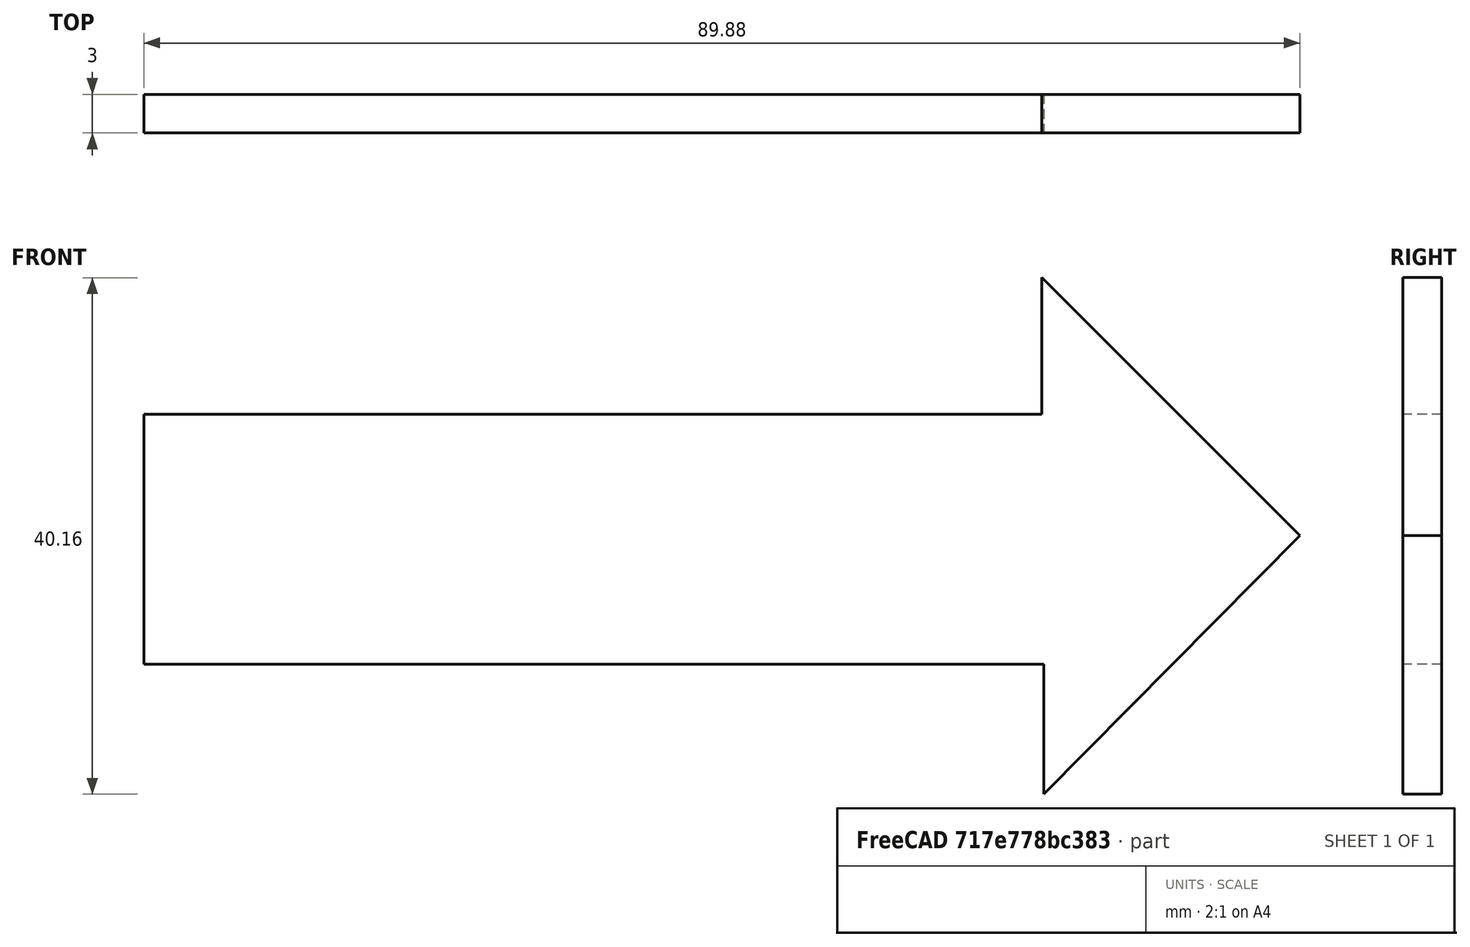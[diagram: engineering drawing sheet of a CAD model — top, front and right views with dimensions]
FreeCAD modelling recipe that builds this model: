
FCSTD DOCUMENT  (FreeCAD 0.21R33694 (Git))
Label: OJT1_T16R02.fletxa
License: All rights reserved
LicenseURL: http://en.wikipedia.org/wiki/All_rights_reserved
objects: Sketcher::SketchObject×1, PartDesign::Pad×1, PartDesign::Body×1
note: 4 computed .brp shape members not serialized (recipe doc carries the construction recipe); baked Part::Feature solids carry a one-line shape summary decoded from their .brp

FEATURE [Sketcher::SketchObject] Sketch
  FullyConstrained = false
  MapMode = 5
  Placement = pos=(0,0,0) rot=(1,0,0;1.5708rad)
  Support = -> [XZ_Plane]
  sketch-geometry (7):
    g0: LineSegment StartX=-29.9479 StartY=9.40476 StartZ=0 EndX=39.8524 EndY=9.40476 EndZ=0
    g1: LineSegment StartX=39.8524 StartY=9.40476 StartZ=0 EndX=39.8524 EndY=20.0415 EndZ=0
    g2: LineSegment StartX=39.8524 StartY=20.0415 StartZ=0 EndX=59.9287 EndY=0 EndZ=0
    g3: LineSegment StartX=59.9287 StartY=0 StartZ=0 EndX=40.0154 EndY=-20.1171 EndZ=0
    g4: LineSegment StartX=40.0154 StartY=-20.1171 StartZ=0 EndX=40.0154 EndY=-10.0238 EndZ=0
    g5: LineSegment StartX=40.0154 StartY=-10.0238 StartZ=0 EndX=-29.9479 EndY=-10.0238 EndZ=0
    g6: LineSegment StartX=-29.9479 StartY=-10.0238 StartZ=0 EndX=-29.9479 EndY=9.40476 EndZ=0
  constraints (13):
    c: Horizontal(g0)
    c: Coincident(g0,g1)
    c: Vertical(g1)
    c: Coincident(g1,g2)
    c: PointOnObject(g2,g-1)
    c: Coincident(g2,g3)
    c: Coincident(g3,g4)
    c: Vertical(g4)
    c: Coincident(g4,g5)
    c: Horizontal(g5)
    c: Coincident(g5,g6)
    c: Coincident(g6,g0)
    c: Vertical(g6)
FEATURE [PartDesign::Pad] Pad
  Direction = (0,-1,2e-16)
  Length = 3
  Length2 = 10
  Placement = pos=(0,0,0) rot=(1,0,0;1.5708rad)
  Profile = -> Sketch
  ReferenceAxis = -> Sketch [N_Axis]
  Refine = true
  Type = 0
FEATURE [PartDesign::Body] Body
  Group = -> [Sketch,Pad]
  Origin = -> Origin
  Tip = -> Pad
